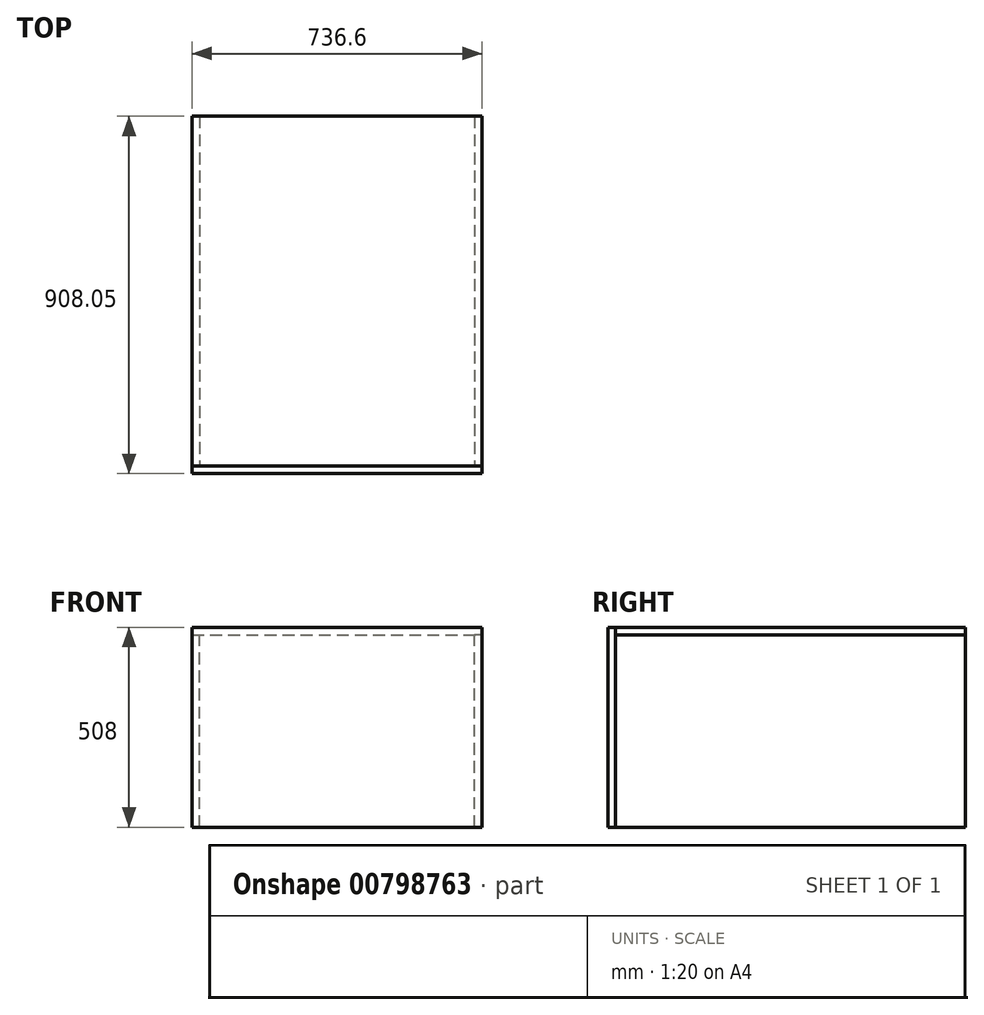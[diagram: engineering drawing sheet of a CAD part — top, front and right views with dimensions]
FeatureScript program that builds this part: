
annotation { "Feature Type Name" : "Feature", "Feature Type Description" : "" }
export const myFeature = defineFeature(function(context is Context, id is Id, definition is map)
    precondition{}
    {
        {
            var Q0;
            Q0=qCreatedBy(makeId("Top.planeOp"),FACE);
            var sketch = newSketch(context, id + "F0", { "sketchPlane" : qUnion([Q0])});
            skLineSegment(sketch, "E0.bottom", {"start": v(0, 0) * mm, "end": v(736.6, 0) * mm});
            skLineSegment(sketch, "E0.top", {"start": v(0, 889) * mm, "end": v(736.6, 889) * mm});
            skLineSegment(sketch, "E0.left", {"start": v(0, 0) * mm, "end": v(0, 889) * mm});
            skLineSegment(sketch, "E0.right", {"start": v(736.6, 0) * mm, "end": v(736.6, 889) * mm});
            skSolve(sketch);
        }
        {
            var Q0;
            Q0=makeQuery(id+"F0.imprint","IMPRINT",FACE,{"disambiguationData":[TD([[makeQuery(id+"F0.imprint","IMPRINT",EDGE,{"derivedFrom":sQuery(id+"F0.wireOp",EDGE,"E0.bottom")}),1.0]])]});
            extrude(context, id + "F1", {"entities" : qUnion([Q0]), "oppositeDirection" : true, "depth" : 19.05 * mm, "offsetDistance" : 25.4 * mm});
        }
        {
            var Q0;
            Q0=makeQuery(id+"F1.opExtrude","SWEPT_FACE",FACE,{"disambiguationData":[OSD([sQuery(id+"F0.wireOp",EDGE,"E0.bottom")])]});
            var sketch = newSketch(context, id + "F2", { "sketchPlane" : qUnion([Q0])});
            skLineSegment(sketch, "E1.bottom", {"start": v(736.6, 0) * mm, "end": v(0, 0) * mm});
            skLineSegment(sketch, "E1.top", {"start": v(736.6, -508) * mm, "end": v(0, -508) * mm});
            skLineSegment(sketch, "E1.left", {"start": v(736.6, 0) * mm, "end": v(736.6, -508) * mm});
            skLineSegment(sketch, "E1.right", {"start": v(0, 0) * mm, "end": v(0, -508) * mm});
            skSolve(sketch);
        }
        {
            var Q0;
            Q0 = qSketchRegion(id + "F2", true);
            extrude(context, id + "F3", {"entities" : qUnion([Q0]), "depth" : 19.05 * mm, "offsetDistance" : 25.4 * mm});
        }
        {
            var Q0;
            Q0=makeQuery(id+"F3.opExtrude","CAP_FACE",FACE,{"disambiguationData":[OSD([sQuery(id+"F2.wireOp",EDGE,"E1.bottom"),sQuery(id+"F2.wireOp",EDGE,"E1.top"),sQuery(id+"F2.wireOp",EDGE,"E1.left"),sQuery(id+"F2.wireOp",EDGE,"E1.right")])],"isStart":true});
            var sketch = newSketch(context, id + "F4", { "sketchPlane" : qUnion([Q0])});
            skLineSegment(sketch, "E2.bottom", {"start": v(0, -508) * mm, "end": v(-19.05, -508) * mm});
            skLineSegment(sketch, "E2.top", {"start": v(0, -19.46) * mm, "end": v(-19.05, -19.46) * mm});
            skLineSegment(sketch, "E2.left", {"start": v(0, -508) * mm, "end": v(0, -19.46) * mm});
            skLineSegment(sketch, "E2.right", {"start": v(-19.05, -508) * mm, "end": v(-19.05, -19.46) * mm});
            skLineSegment(sketch, "E3.bottom", {"start": v(-736.6, -508) * mm, "end": v(-717.55, -508) * mm});
            skLineSegment(sketch, "E3.top", {"start": v(-736.6, -19.46) * mm, "end": v(-717.55, -19.46) * mm});
            skLineSegment(sketch, "E3.left", {"start": v(-736.6, -508) * mm, "end": v(-736.6, -19.46) * mm});
            skLineSegment(sketch, "E3.right", {"start": v(-717.55, -508) * mm, "end": v(-717.55, -19.46) * mm});
            skSolve(sketch);
        }
        {
            var Q0;
            Q0 = qSketchRegion(id + "F4", true);
            extrude(context, id + "F5", {"entities" : qUnion([Q0]), "depth" : 889 * mm, "offsetDistance" : 25.4 * mm});
        }
    });
